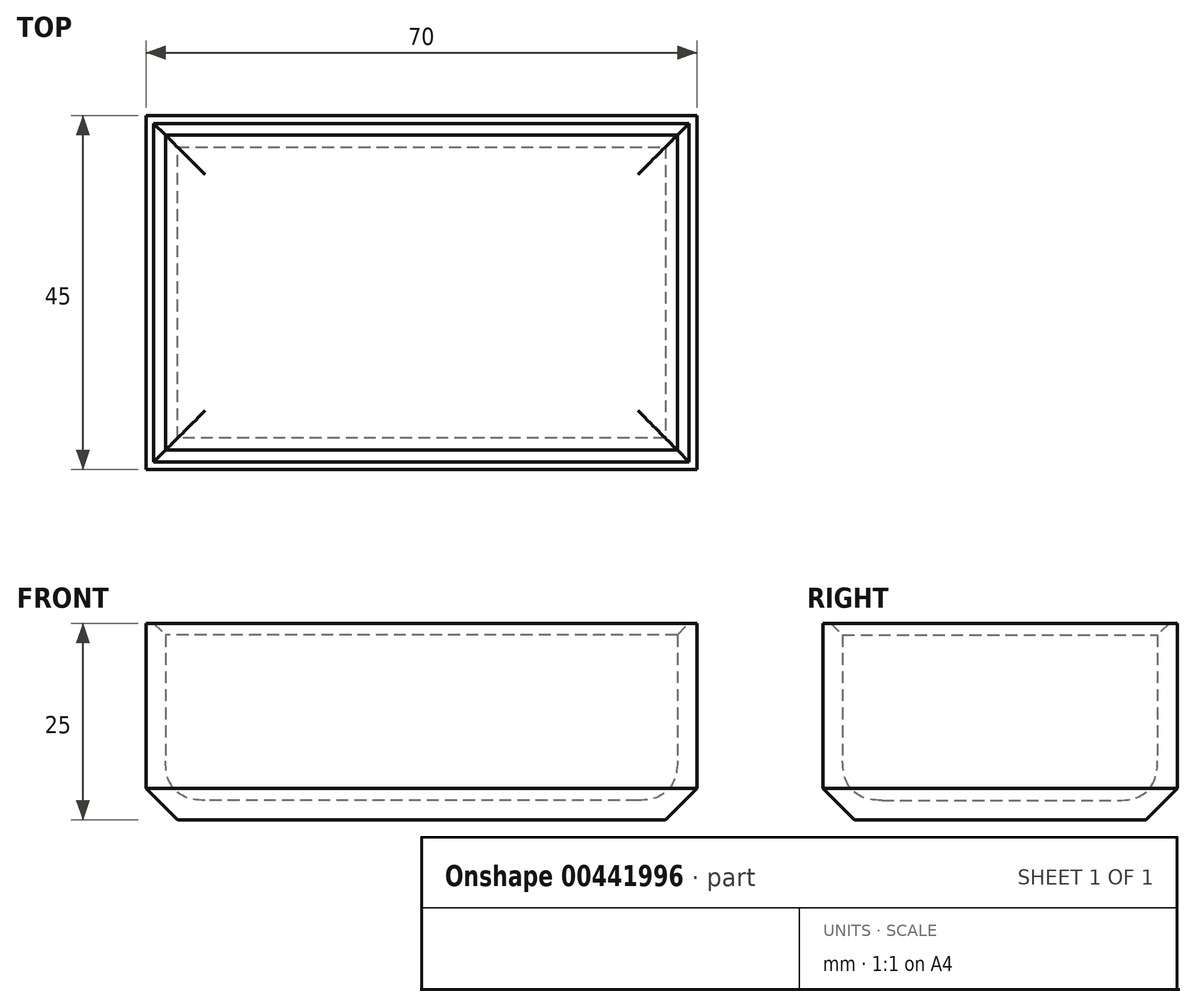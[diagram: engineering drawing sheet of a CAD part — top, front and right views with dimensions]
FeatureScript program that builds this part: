
annotation { "Feature Type Name" : "Feature", "Feature Type Description" : "" }
export const myFeature = defineFeature(function(context is Context, id is Id, definition is map)
    precondition{}
    {
        {
            var Q0;
            Q0=qCreatedBy(makeId("Top.planeOp"),FACE);
            var sketch = newSketch(context, id + "F0", { "sketchPlane" : qUnion([Q0])});
            skLineSegment(sketch, "E0", {"start": v(44.3, -17) * mm, "end": v(44.3, -62) * mm});
            skLineSegment(sketch, "E1", {"start": v(44.3, -62) * mm, "end": v(-25.7, -62) * mm});
            skLineSegment(sketch, "E2", {"start": v(-25.7, -62) * mm, "end": v(-25.7, -17) * mm});
            skLineSegment(sketch, "E3", {"start": v(-25.7, -17) * mm, "end": v(44.3, -17) * mm});
            skSolve(sketch);
        }
        {
            var Q0;
            Q0=makeQuery(id+"F0.imprint","IMPRINT",FACE,{"disambiguationData":[TD([[makeQuery(id+"F0.imprint","IMPRINT",EDGE,{"derivedFrom":sQuery(id+"F0.wireOp",EDGE,"E0")}),-1.0]])]});
            extrude(context, id + "F1", {"entities" : qUnion([Q0]), "depth" : 25 * mm});
        }
        {
            var Q0;
            Q0=makeQuery(id+"F1.opExtrude","CAP_FACE",FACE,{"disambiguationData":[OSD([sQuery(id+"F0.wireOp",EDGE,"E0"),sQuery(id+"F0.wireOp",EDGE,"E1"),sQuery(id+"F0.wireOp",EDGE,"E2"),sQuery(id+"F0.wireOp",EDGE,"E3")])],"isStart":false});
            shell(context, id + "F2", {"entities" : qUnion([Q0]), "thickness" : 2.5 * mm});
        }
        {
            var Q0;
            {var subQ0=sQuery(id+"F0.wireOp",EDGE,"E2");Q0=makeQuery(id+"F2.opShell","OFFSET_EDGE",EDGE,{"disambiguationData":[OSD([subQ0]),TDD([makeQuery(id+"F1.opExtrude","CAP_EDGE",EDGE,{"disambiguationData":[OSD([subQ0])],"isStart":true})])]});}
            var Q1;
            {var subQ0=sQuery(id+"F0.wireOp",EDGE,"E3");Q1=makeQuery(id+"F2.opShell","OFFSET_EDGE",EDGE,{"disambiguationData":[OSD([subQ0]),TDD([makeQuery(id+"F1.opExtrude","CAP_EDGE",EDGE,{"disambiguationData":[OSD([subQ0])],"isStart":true})])]});}
            var Q2;
            {var subQ0=sQuery(id+"F0.wireOp",EDGE,"E0");Q2=makeQuery(id+"F2.opShell","OFFSET_EDGE",EDGE,{"disambiguationData":[OSD([subQ0]),TDD([makeQuery(id+"F1.opExtrude","CAP_EDGE",EDGE,{"disambiguationData":[OSD([subQ0])],"isStart":true})])]});}
            var Q3;
            {var subQ0=sQuery(id+"F0.wireOp",EDGE,"E1");Q3=makeQuery(id+"F2.opShell","OFFSET_EDGE",EDGE,{"disambiguationData":[OSD([subQ0]),TDD([makeQuery(id+"F1.opExtrude","CAP_EDGE",EDGE,{"disambiguationData":[OSD([subQ0])],"isStart":true})])]});}
            fillet(context, id + "F3", {"entities" : qUnion([Q0, Q1, Q2, Q3]), "radius" : 5 * mm, "tangentPropagation" : true, "rho" : 0.5, "crossSection" : FilletCrossSection.CONIC, "allowEdgeOverflow" : false});
        }
        {
            var Q0;
            Q0=makeQuery(id+"F1.opExtrude","CAP_EDGE",EDGE,{"disambiguationData":[OSD([sQuery(id+"F0.wireOp",EDGE,"E1")])],"isStart":true});
            var Q1;
            Q1=makeQuery(id+"F1.opExtrude","CAP_EDGE",EDGE,{"disambiguationData":[OSD([sQuery(id+"F0.wireOp",EDGE,"E2")])],"isStart":true});
            var Q2;
            Q2=makeQuery(id+"F1.opExtrude","CAP_EDGE",EDGE,{"disambiguationData":[OSD([sQuery(id+"F0.wireOp",EDGE,"E0")])],"isStart":true});
            var Q3;
            Q3=makeQuery(id+"F1.opExtrude","CAP_EDGE",EDGE,{"disambiguationData":[OSD([sQuery(id+"F0.wireOp",EDGE,"E3")])],"isStart":true});
            chamfer(context, id + "F4", {"entities" : qUnion([Q0, Q1, Q2, Q3]), "width" : 4 * mm, "tangentPropagation" : true});
        }
        {
            var Q0;
            {var subQ0=sQuery(id+"F0.wireOp",EDGE,"E3");Q0=makeQuery(id+"F2.opShell","OFFSET_EDGE",EDGE,{"disambiguationData":[OSD([subQ0]),TDD([makeQuery(id+"F1.opExtrude","CAP_EDGE",EDGE,{"disambiguationData":[OSD([subQ0])],"isStart":false})])]});}
            var Q1;
            {var subQ0=sQuery(id+"F0.wireOp",EDGE,"E2");Q1=makeQuery(id+"F2.opShell","OFFSET_EDGE",EDGE,{"disambiguationData":[OSD([subQ0]),TDD([makeQuery(id+"F1.opExtrude","CAP_EDGE",EDGE,{"disambiguationData":[OSD([subQ0])],"isStart":false})])]});}
            var Q2;
            {var subQ0=sQuery(id+"F0.wireOp",EDGE,"E1");Q2=makeQuery(id+"F2.opShell","OFFSET_EDGE",EDGE,{"disambiguationData":[OSD([subQ0]),TDD([makeQuery(id+"F1.opExtrude","CAP_EDGE",EDGE,{"disambiguationData":[OSD([subQ0])],"isStart":false})])]});}
            var Q3;
            {var subQ0=sQuery(id+"F0.wireOp",EDGE,"E0");Q3=makeQuery(id+"F2.opShell","OFFSET_EDGE",EDGE,{"disambiguationData":[OSD([subQ0]),TDD([makeQuery(id+"F1.opExtrude","CAP_EDGE",EDGE,{"disambiguationData":[OSD([subQ0])],"isStart":false})])]});}
            chamfer(context, id + "F5", {"entities" : qUnion([Q0, Q1, Q2, Q3]), "width" : 1.5 * mm, "tangentPropagation" : true});
        }
    });
